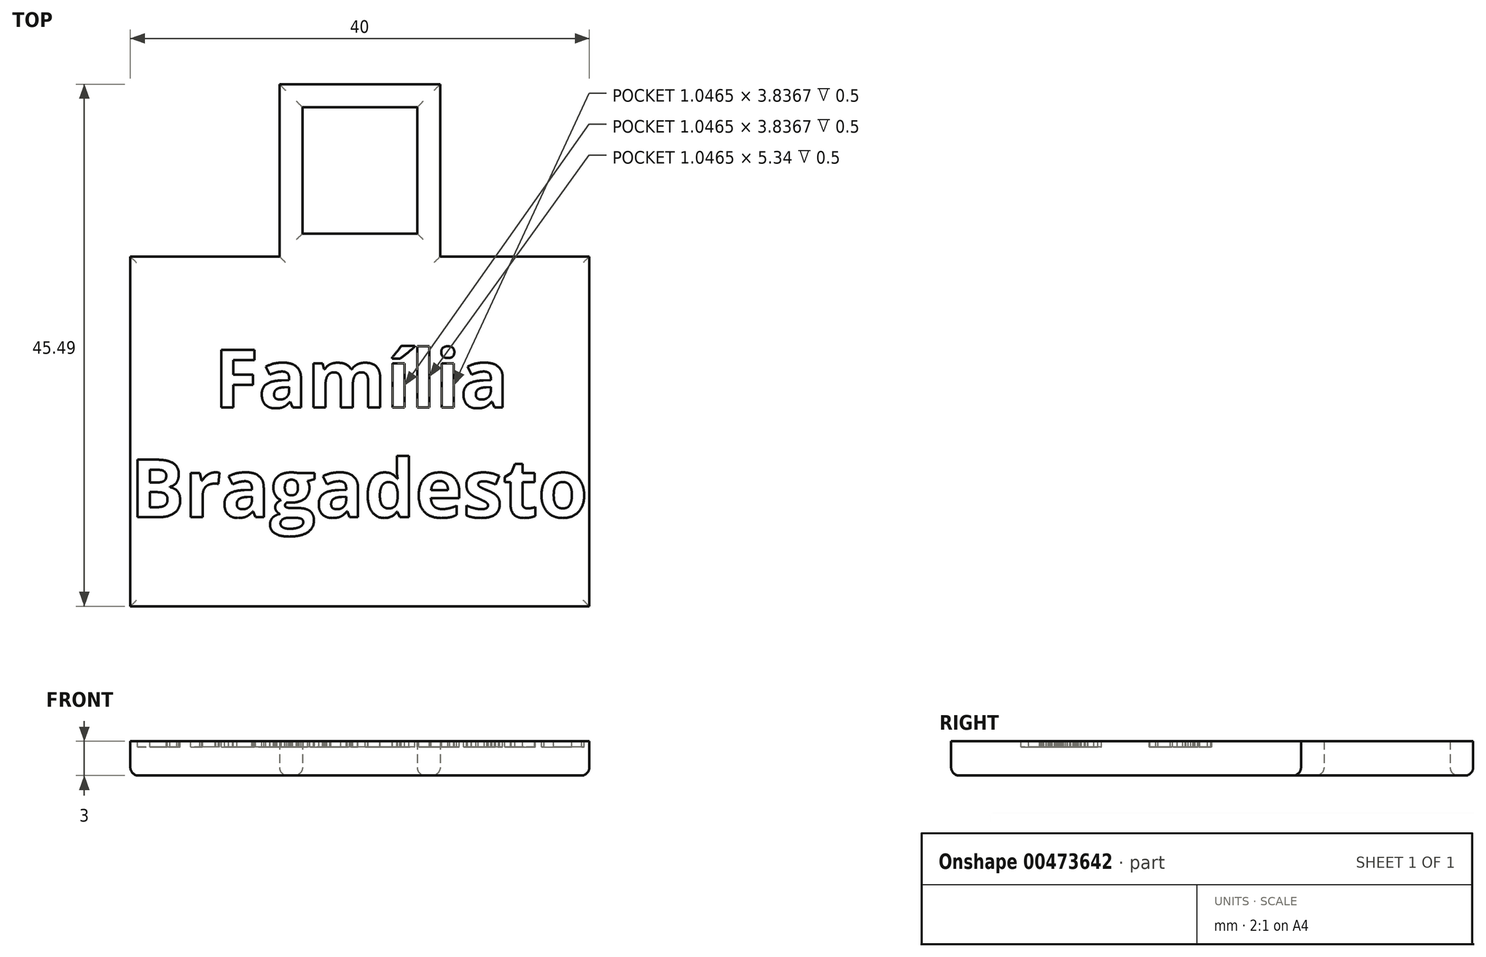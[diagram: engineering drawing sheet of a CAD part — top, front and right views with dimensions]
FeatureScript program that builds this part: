
annotation { "Feature Type Name" : "Feature", "Feature Type Description" : "" }
export const myFeature = defineFeature(function(context is Context, id is Id, definition is map)
    precondition{}
    {
        {
            var Q0;
            Q0=qCreatedBy(makeId("Top.planeOp"),FACE);
            var sketch = newSketch(context, id + "F0", { "sketchPlane" : qUnion([Q0])});
            skLineSegment(sketch, "E0.top", {"start": v(-20.04, -8.3) * mm, "end": v(19.96, -8.3) * mm});
            skLineSegment(sketch, "E0.left", {"start": v(-20.04, 22.2) * mm, "end": v(-20.04, -8.3) * mm});
            skLineSegment(sketch, "E0.right", {"start": v(19.96, 22.2) * mm, "end": v(19.96, -8.3) * mm});
            skLineSegment(sketch, "E1", {"start": v(-20.04, 22.2) * mm, "end": v(-7.04, 22.2) * mm});
            skLineSegment(sketch, "E2", {"start": v(-7.04, 22.2) * mm, "end": v(-7.04, 37.2) * mm});
            skLineSegment(sketch, "E3", {"start": v(19.96, 22.2) * mm, "end": v(6.96, 22.2) * mm});
            skLineSegment(sketch, "E4", {"start": v(6.96, 22.2) * mm, "end": v(6.96, 37.2) * mm});
            skLineSegment(sketch, "E5", {"start": v(6.96, 37.2) * mm, "end": v(-7.04, 37.2) * mm});
            skLineSegment(sketch, "E6.0", {"start": v(4.96, 35.2) * mm, "end": v(-5.04, 35.2) * mm});
            skLineSegment(sketch, "E6.1", {"start": v(4.96, 24.2) * mm, "end": v(4.96, 35.2) * mm});
            skLineSegment(sketch, "E6.2", {"start": v(-5.04, 24.2) * mm, "end": v(4.96, 24.2) * mm});
            skLineSegment(sketch, "E6.3", {"start": v(-5.04, 24.2) * mm, "end": v(-5.04, 35.2) * mm});
            skSolve(sketch);
        }
        {
            var Q0;
            Q0=makeQuery(id+"F0.imprint","IMPRINT",FACE,{"disambiguationData":[TD([[makeQuery(id+"F0.imprint","IMPRINT",EDGE,{"derivedFrom":sQuery(id+"F0.wireOp",EDGE,"E0.top")}),1.0]])]});
            extrude(context, id + "F1", {"entities" : qUnion([Q0]), "depth" : 3 * mm, "offsetDistance" : 25 * mm});
        }
        {
            var Q0;
            Q0=makeQuery(id+"F1.opExtrude","CAP_FACE",FACE,{"disambiguationData":[OSD([sQuery(id+"F0.wireOp",EDGE,"sQfz1dRQ-c3YA-cxI6-qmPz-qNKNI9TLlWNe.bottom"),sQuery(id+"F0.wireOp",EDGE,"sQfz1dRQ-c3YA-cxI6-qmPz-qNKNI9TLlWNe.left"),sQuery(id+"F0.wireOp",EDGE,"sQfz1dRQ-c3YA-cxI6-qmPz-qNKNI9TLlWNe.right"),sQuery(id+"F0.wireOp",EDGE,"okDgpMo1-AZeH-f98o-D7jR-ALTmc36VbUzS.bottom"),sQuery(id+"F0.wireOp",EDGE,"okDgpMo1-AZeH-f98o-D7jR-ALTmc36VbUzS.top"),sQuery(id+"F0.wireOp",EDGE,"okDgpMo1-AZeH-f98o-D7jR-ALTmc36VbUzS.left"),sQuery(id+"F0.wireOp",EDGE,"okDgpMo1-AZeH-f98o-D7jR-ALTmc36VbUzS.right"),sQuery(id+"F0.wireOp",EDGE,"E0.bottom"),sQuery(id+"F0.wireOp",EDGE,"E0.top"),sQuery(id+"F0.wireOp",EDGE,"E0.left"),sQuery(id+"F0.wireOp",EDGE,"E0.right"),sQuery(id+"F0.wireOp",EDGE,"JawxHhje-faLj-zHVJ-nq1w-yCwpkV4hGCtU"),sQuery(id+"F0.wireOp",EDGE,"GakTh1Vh-VPFx-4KnP-zQR7-rtxN0rmuNG0S"),sQuery(id+"F0.wireOp",EDGE,"a6408a47-cff2-428e-8156-9cfd21a05fc8.trimOffspring")])],"isStart":false});
            var sketch = newSketch(context, id + "F2", { "sketchPlane" : qUnion([Q0])});
            skText(sketch, "E7", { "text": "    Família \nBragadesto", "fontName": "OpenSans-Bold.ttf"});
            const initialGuessF2  = {"E7": [-0.02004, 0.00903, 1, 0, 0.00506]};
            skSetInitialGuess(sketch, initialGuessF2);
            skSolve(sketch);
        }
        {
            var Q0;
            Q0 = qSketchRegion(id + "F2", true);
            extrude(context, id + "F3", {"entities" : qUnion([Q0]), "operationType" : NewBodyOperationType.REMOVE, "oppositeDirection" : true, "depth" : 0.5 * mm, "offsetDistance" : 25 * mm});
        }
        {
            var Q0;
            Q0=makeQuery(id+"F1.opExtrude","CAP_FACE",FACE,{"disambiguationData":[OSD([sQuery(id+"F0.wireOp",EDGE,"sQfz1dRQ-c3YA-cxI6-qmPz-qNKNI9TLlWNe.bottom"),sQuery(id+"F0.wireOp",EDGE,"sQfz1dRQ-c3YA-cxI6-qmPz-qNKNI9TLlWNe.left"),sQuery(id+"F0.wireOp",EDGE,"sQfz1dRQ-c3YA-cxI6-qmPz-qNKNI9TLlWNe.right"),sQuery(id+"F0.wireOp",EDGE,"okDgpMo1-AZeH-f98o-D7jR-ALTmc36VbUzS.bottom"),sQuery(id+"F0.wireOp",EDGE,"okDgpMo1-AZeH-f98o-D7jR-ALTmc36VbUzS.top"),sQuery(id+"F0.wireOp",EDGE,"okDgpMo1-AZeH-f98o-D7jR-ALTmc36VbUzS.left"),sQuery(id+"F0.wireOp",EDGE,"okDgpMo1-AZeH-f98o-D7jR-ALTmc36VbUzS.right"),sQuery(id+"F0.wireOp",EDGE,"E0.bottom"),sQuery(id+"F0.wireOp",EDGE,"E0.top"),sQuery(id+"F0.wireOp",EDGE,"E0.left"),sQuery(id+"F0.wireOp",EDGE,"E0.right"),sQuery(id+"F0.wireOp",EDGE,"JawxHhje-faLj-zHVJ-nq1w-yCwpkV4hGCtU"),sQuery(id+"F0.wireOp",EDGE,"GakTh1Vh-VPFx-4KnP-zQR7-rtxN0rmuNG0S"),sQuery(id+"F0.wireOp",EDGE,"a6408a47-cff2-428e-8156-9cfd21a05fc8.trimOffspring")])],"isStart":true});
            fillet(context, id + "F4", {"entities" : qUnion([Q0]), "radius" : 0.7 * mm, "tangentPropagation" : true, "allowEdgeOverflow" : false});
        }
    });
